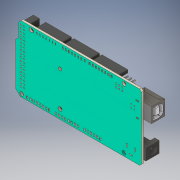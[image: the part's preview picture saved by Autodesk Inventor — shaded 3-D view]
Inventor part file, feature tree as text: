
AUTODESK INVENTOR PART (.ipt)
format: ipt  version: 2019 (Build 230136000, 136)  size: 2,321,408 bytes
history: mixed  units: in
note: dims shown in document units (in); Inventor stores cm internally (conversion verified against a paired STEP export)
features: other x1, extrude x1, sketch x1, fillet x1, imported_body x1
ambient origin geometry x8: Origin, YZ Plane, XZ Plane, XY Plane, X Axis, Y Axis, Z Axis, Center Point
bodies: Solid1 (imported_parasolid)
feature tree (5):
  other  "ArduinoMega.SLDPRT"
  extrude  "Extrusion1"  Depth=0.25in
  sketch  "Sketch1"  dims[d0=0.45in d1=0.25in d2=0.25in d3=0.2633in d4=0.22in d5=0.22in d6=0.2633in d8=0.2in d9=0.001in d10=0.0in]
  fillet  "Fillet5"  Radius=0.25in
  imported_body  NMx_Import_Brep_tag  [imported B-rep: ~186 faces, bbox_mm=[103.4288, 53.4162, 10.0838]]
